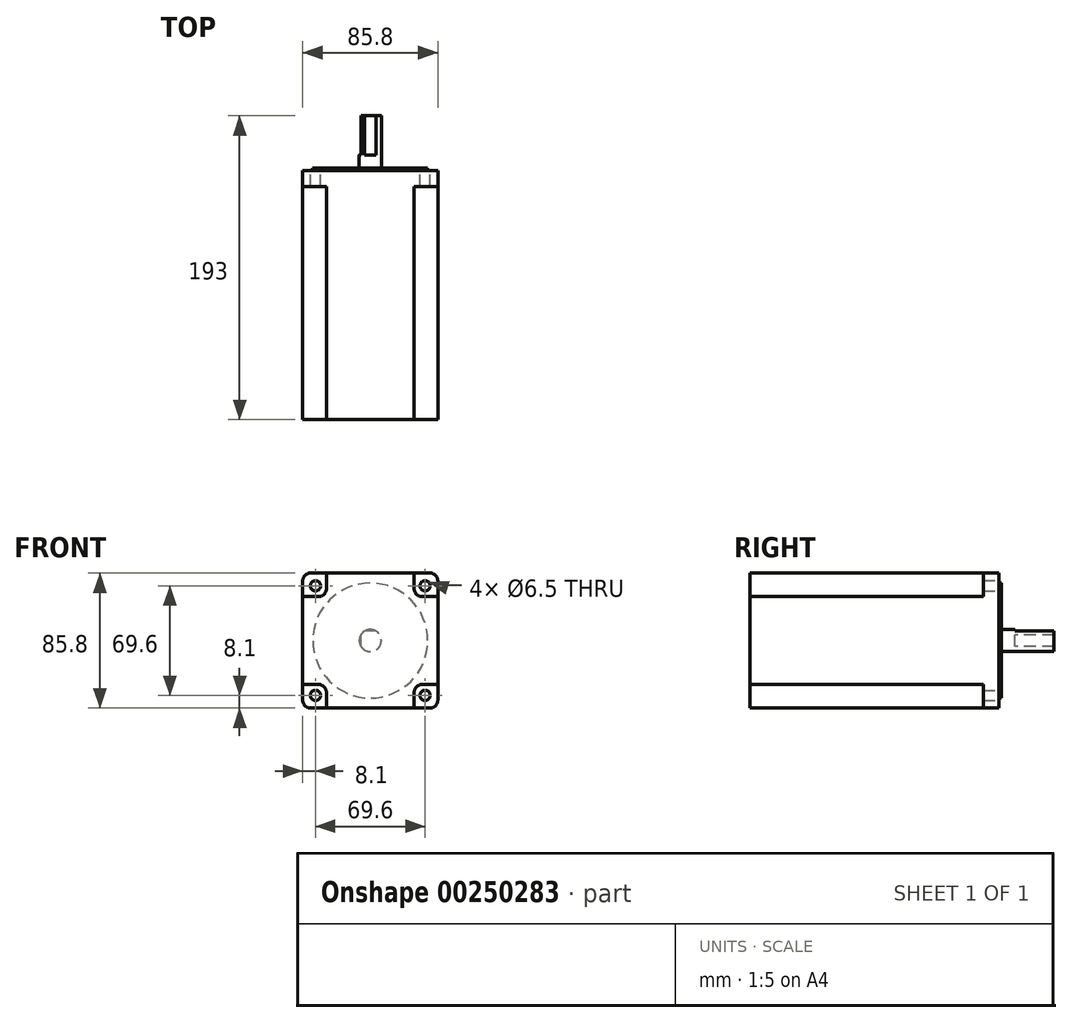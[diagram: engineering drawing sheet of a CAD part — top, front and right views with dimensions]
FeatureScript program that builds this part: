
annotation { "Feature Type Name" : "Feature", "Feature Type Description" : "" }
export const myFeature = defineFeature(function(context is Context, id is Id, definition is map)
    precondition{}
    {
        {
            var Q0;
            Q0=qCreatedBy(makeId("Front.planeOp"),FACE);
            var sketch = newSketch(context, id + "F0", { "sketchPlane" : qUnion([Q0])});
            skLineSegment(sketch, "E0.bottom", {"start": v(-37.9, 42.9) * mm, "end": v(37.9, 42.9) * mm});
            skLineSegment(sketch, "E0.top", {"start": v(-37.9, -42.9) * mm, "end": v(37.9, -42.9) * mm});
            skLineSegment(sketch, "E0.left", {"start": v(-42.9, 37.9) * mm, "end": v(-42.9, -37.9) * mm});
            skLineSegment(sketch, "E0.right", {"start": v(42.9, 37.9) * mm, "end": v(42.9, -37.9) * mm});
            skArc(sketch, "E1.filletArc", {"start": v(-42.9, -37.9) * mm, "mid": v(-41.44, -41.44) * mm, "end": v(-37.9, -42.9) * mm});
            skPoint(sketch, "E2.visualSharp", {"position": v(-42.9, 42.9) * mm});
            skArc(sketch, "E2.filletArc", {"start": v(-37.9, 42.9) * mm, "mid": v(-41.44, 41.44) * mm, "end": v(-42.9, 37.9) * mm});
            skPoint(sketch, "E3.visualSharp", {"position": v(42.9, 42.9) * mm});
            skArc(sketch, "E3.filletArc", {"start": v(42.9, 37.9) * mm, "mid": v(41.44, 41.44) * mm, "end": v(37.9, 42.9) * mm});
            skPoint(sketch, "E4.visualSharp", {"position": v(42.9, -42.9) * mm});
            skArc(sketch, "E4.filletArc", {"start": v(37.9, -42.9) * mm, "mid": v(41.44, -41.44) * mm, "end": v(42.9, -37.9) * mm});
            skSolve(sketch);
        }
        {
            var Q0;
            Q0=makeQuery(id+"F0.imprint","IMPRINT",FACE,{"disambiguationData":[TD([[makeQuery(id+"F0.imprint","IMPRINT",EDGE,{"derivedFrom":sQuery(id+"F0.wireOp",EDGE,"E0.bottom")}),-1.0]])]});
            extrude(context, id + "F1", {"entities" : qUnion([Q0]), "depth" : 158 * mm});
        }
        {
            var Q0;
            Q0=makeQuery(id+"F1.opExtrude","CAP_FACE",FACE,{"disambiguationData":[OSD([sQuery(id+"F0.wireOp",EDGE,"E0.bottom"),sQuery(id+"F0.wireOp",EDGE,"E0.top"),sQuery(id+"F0.wireOp",EDGE,"E0.left"),sQuery(id+"F0.wireOp",EDGE,"E0.right"),sQuery(id+"F0.wireOp",EDGE,"E1.filletArc"),sQuery(id+"F0.wireOp",EDGE,"E2.filletArc"),sQuery(id+"F0.wireOp",EDGE,"E3.filletArc"),sQuery(id+"F0.wireOp",EDGE,"E4.filletArc")])],"isStart":false});
            var sketch = newSketch(context, id + "F2", { "sketchPlane" : qUnion([Q0])});
            skLineSegment(sketch, "E5.bottom", {"start": v(27.9, 42.9) * mm, "end": v(42.9, 42.9) * mm});
            skLineSegment(sketch, "E5.top", {"start": v(27.9, 27.9) * mm, "end": v(42.9, 27.9) * mm});
            skLineSegment(sketch, "E5.left", {"start": v(27.9, 42.9) * mm, "end": v(27.9, 27.9) * mm});
            skLineSegment(sketch, "E5.right", {"start": v(42.9, 42.9) * mm, "end": v(42.9, 27.9) * mm});
            skLineSegment(sketch, "E6.MirrorCS", {"start": v(-27.9, 42.9) * mm, "end": v(-42.9, 42.9) * mm});
            skLineSegment(sketch, "E7.MirrorCS", {"start": v(-27.9, 27.9) * mm, "end": v(-42.9, 27.9) * mm});
            skLineSegment(sketch, "E8.MirrorCS", {"start": v(-42.9, 42.9) * mm, "end": v(-42.9, 27.9) * mm});
            skLineSegment(sketch, "E9.MirrorCS", {"start": v(-27.9, 42.9) * mm, "end": v(-27.9, 27.9) * mm});
            skLineSegment(sketch, "E10.MirrorCS", {"start": v(-27.9, -42.9) * mm, "end": v(-27.9, -27.9) * mm});
            skLineSegment(sketch, "E11.MirrorCS", {"start": v(-27.9, -42.9) * mm, "end": v(-42.9, -42.9) * mm});
            skLineSegment(sketch, "E12.MirrorCS", {"start": v(-27.9, -27.9) * mm, "end": v(-42.9, -27.9) * mm});
            skLineSegment(sketch, "E13.MirrorCS", {"start": v(-42.9, -42.9) * mm, "end": v(-42.9, -27.9) * mm});
            skLineSegment(sketch, "E14.MirrorCS", {"start": v(42.9, -42.9) * mm, "end": v(42.9, -27.9) * mm});
            skLineSegment(sketch, "E15.MirrorCS", {"start": v(27.9, -27.9) * mm, "end": v(42.9, -27.9) * mm});
            skLineSegment(sketch, "E16.MirrorCS", {"start": v(27.9, -42.9) * mm, "end": v(42.9, -42.9) * mm});
            skLineSegment(sketch, "E17.MirrorCS", {"start": v(27.9, -42.9) * mm, "end": v(27.9, -27.9) * mm});
            skSolve(sketch);
        }
        {
            var Q0;
            Q0=qSketchRegion(id+"F2",true);
            var Q1;
            Q1=makeQuery(id+"F1.opExtrude","CAP_FACE",FACE,{"disambiguationData":[OSD([sQuery(id+"F0.wireOp",EDGE,"E0.bottom"),sQuery(id+"F0.wireOp",EDGE,"E0.top"),sQuery(id+"F0.wireOp",EDGE,"E0.left"),sQuery(id+"F0.wireOp",EDGE,"E0.right"),sQuery(id+"F0.wireOp",EDGE,"E1.filletArc"),sQuery(id+"F0.wireOp",EDGE,"E2.filletArc"),sQuery(id+"F0.wireOp",EDGE,"E3.filletArc"),sQuery(id+"F0.wireOp",EDGE,"E4.filletArc")])],"isStart":false});
            extrude(context, id + "F3", {"entities" : qUnion([Q0]), "operationType" : NewBodyOperationType.REMOVE, "oppositeDirection" : true, "endBoundEntityFace" : qUnion([Q1]), "depth" : 148 * mm});
        }
        {
            var Q0;
            Q0=makeQuery(id+"F1.opExtrude","CAP_FACE",FACE,{"disambiguationData":[OSD([sQuery(id+"F0.wireOp",EDGE,"E0.bottom"),sQuery(id+"F0.wireOp",EDGE,"E0.top"),sQuery(id+"F0.wireOp",EDGE,"E0.left"),sQuery(id+"F0.wireOp",EDGE,"E0.right"),sQuery(id+"F0.wireOp",EDGE,"E1.filletArc"),sQuery(id+"F0.wireOp",EDGE,"E2.filletArc"),sQuery(id+"F0.wireOp",EDGE,"E3.filletArc"),sQuery(id+"F0.wireOp",EDGE,"E4.filletArc")])],"isStart":true});
            var sketch = newSketch(context, id + "F4", { "sketchPlane" : qUnion([Q0])});
            skCircle(sketch, "E18", {"center": v(34.8, 34.8) * mm, "radius": 3.25 * mm});
            skCircle(sketch, "E19.MirrorC", {"center": v(-34.8, 34.8) * mm, "radius": 3.25 * mm});
            skCircle(sketch, "E20.MirrorC", {"center": v(34.8, -34.8) * mm, "radius": 3.25 * mm});
            skCircle(sketch, "E21.MirrorC", {"center": v(-34.8, -34.8) * mm, "radius": 3.25 * mm});
            skSolve(sketch);
        }
        {
            var Q0;
            Q0=qSketchRegion(id+"F4",true);
            extrude(context, id + "F5", {"entities" : qUnion([Q0]), "operationType" : NewBodyOperationType.REMOVE, "endBound" : BoundingType.UP_TO_NEXT, "oppositeDirection" : true, "depth" : 25 * mm});
        }
        {
            var Q0;
            Q0=makeQuery(id+"F3.boolean.opBoolean","COPY",EDGE,{"derivedFrom":makeQuery(id+"F3.opExtrude","SWEPT_EDGE",EDGE,{"disambiguationData":[OSD([sQuery(id+"F0.wireOp",EDGE,"E0.left"),sQuery(id+"F2.wireOp",EDGE,"E8.MirrorCS"),sQuery(id+"F2.wireOp",EDGE,"E7.MirrorCS")])]})});
            var Q1;
            Q1=makeQuery(id+"F3.boolean.opBoolean","COPY",EDGE,{"derivedFrom":makeQuery(id+"F3.opExtrude","SWEPT_EDGE",EDGE,{"disambiguationData":[OSD([sQuery(id+"F0.wireOp",EDGE,"E0.left"),sQuery(id+"F2.wireOp",EDGE,"E13.MirrorCS"),sQuery(id+"F2.wireOp",EDGE,"E12.MirrorCS")])]})});
            var Q2;
            Q2=makeQuery(id+"F3.boolean.opBoolean","COPY",EDGE,{"derivedFrom":makeQuery(id+"F3.opExtrude","SWEPT_EDGE",EDGE,{"disambiguationData":[OSD([sQuery(id+"F2.wireOp",EDGE,"E12.MirrorCS"),sQuery(id+"F2.wireOp",EDGE,"E10.MirrorCS")])]})});
            var Q3;
            Q3=makeQuery(id+"F3.boolean.opBoolean","COPY",EDGE,{"derivedFrom":makeQuery(id+"F3.opExtrude","SWEPT_EDGE",EDGE,{"disambiguationData":[OSD([sQuery(id+"F0.wireOp",EDGE,"E0.top"),sQuery(id+"F2.wireOp",EDGE,"E10.MirrorCS"),sQuery(id+"F2.wireOp",EDGE,"E11.MirrorCS")])]})});
            var Q4;
            Q4=makeQuery(id+"F3.boolean.opBoolean","COPY",EDGE,{"derivedFrom":makeQuery(id+"F3.opExtrude","SWEPT_EDGE",EDGE,{"disambiguationData":[OSD([sQuery(id+"F0.wireOp",EDGE,"E0.top"),sQuery(id+"F2.wireOp",EDGE,"E17.MirrorCS"),sQuery(id+"F2.wireOp",EDGE,"E16.MirrorCS")])]})});
            var Q5;
            Q5=makeQuery(id+"F3.boolean.opBoolean","COPY",EDGE,{"derivedFrom":makeQuery(id+"F3.opExtrude","SWEPT_EDGE",EDGE,{"disambiguationData":[OSD([sQuery(id+"F0.wireOp",EDGE,"E0.bottom"),sQuery(id+"F2.wireOp",EDGE,"E9.MirrorCS"),sQuery(id+"F2.wireOp",EDGE,"E6.MirrorCS")])]})});
            var Q6;
            Q6=makeQuery(id+"F3.boolean.opBoolean","COPY",EDGE,{"derivedFrom":makeQuery(id+"F3.opExtrude","SWEPT_EDGE",EDGE,{"disambiguationData":[OSD([sQuery(id+"F2.wireOp",EDGE,"E17.MirrorCS"),sQuery(id+"F2.wireOp",EDGE,"E15.MirrorCS")])]})});
            var Q7;
            Q7=makeQuery(id+"F3.boolean.opBoolean","COPY",EDGE,{"derivedFrom":makeQuery(id+"F3.opExtrude","SWEPT_EDGE",EDGE,{"disambiguationData":[OSD([sQuery(id+"F0.wireOp",EDGE,"E0.right"),sQuery(id+"F2.wireOp",EDGE,"E14.MirrorCS"),sQuery(id+"F2.wireOp",EDGE,"E15.MirrorCS")])]})});
            var Q8;
            Q8=makeQuery(id+"F3.boolean.opBoolean","COPY",EDGE,{"derivedFrom":makeQuery(id+"F3.opExtrude","SWEPT_EDGE",EDGE,{"disambiguationData":[OSD([sQuery(id+"F0.wireOp",EDGE,"E0.right"),sQuery(id+"F2.wireOp",EDGE,"E5.right"),sQuery(id+"F2.wireOp",EDGE,"E5.top")])]})});
            var Q9;
            Q9=makeQuery(id+"F3.boolean.opBoolean","COPY",EDGE,{"derivedFrom":makeQuery(id+"F3.opExtrude","SWEPT_EDGE",EDGE,{"disambiguationData":[OSD([sQuery(id+"F0.wireOp",EDGE,"E0.bottom"),sQuery(id+"F2.wireOp",EDGE,"E5.bottom"),sQuery(id+"F2.wireOp",EDGE,"E5.left")])]})});
            var Q10;
            Q10=makeQuery(id+"F3.boolean.opBoolean","COPY",EDGE,{"derivedFrom":makeQuery(id+"F3.opExtrude","SWEPT_EDGE",EDGE,{"disambiguationData":[OSD([sQuery(id+"F2.wireOp",EDGE,"E5.top"),sQuery(id+"F2.wireOp",EDGE,"E5.left")])]})});
            var Q11;
            Q11=makeQuery(id+"F3.boolean.opBoolean","COPY",EDGE,{"derivedFrom":makeQuery(id+"F3.opExtrude","SWEPT_EDGE",EDGE,{"disambiguationData":[OSD([sQuery(id+"F2.wireOp",EDGE,"E9.MirrorCS"),sQuery(id+"F2.wireOp",EDGE,"E7.MirrorCS")])]})});
            fillet(context, id + "F6", {"entities" : qUnion([Q0, Q1, Q2, Q3, Q4, Q5, Q6, Q7, Q8, Q9, Q10, Q11]), "radius" : 5 * mm, "tangentPropagation" : true, "allowEdgeOverflow" : false});
        }
        {
            var Q0;
            Q0=makeQuery(id+"F1.opExtrude","CAP_FACE",FACE,{"disambiguationData":[OSD([sQuery(id+"F0.wireOp",EDGE,"E0.bottom"),sQuery(id+"F0.wireOp",EDGE,"E0.top"),sQuery(id+"F0.wireOp",EDGE,"E0.left"),sQuery(id+"F0.wireOp",EDGE,"E0.right"),sQuery(id+"F0.wireOp",EDGE,"E1.filletArc"),sQuery(id+"F0.wireOp",EDGE,"E2.filletArc"),sQuery(id+"F0.wireOp",EDGE,"E3.filletArc"),sQuery(id+"F0.wireOp",EDGE,"E4.filletArc")])],"isStart":true});
            var sketch = newSketch(context, id + "F7", { "sketchPlane" : qUnion([Q0])});
            skCircle(sketch, "E22", {"center": v(0, 0) * mm, "radius": 36.5 * mm});
            skSolve(sketch);
        }
        {
            var Q0;
            Q0=qSketchRegion(id+"F7",true);
            extrude(context, id + "F8", {"entities" : qUnion([Q0]), "operationType" : NewBodyOperationType.ADD, "depth" : 1.6 * mm});
        }
        {
            var Q0;
            Q0=makeQuery(id+"F1.opExtrude","CAP_FACE",FACE,{"disambiguationData":[OSD([sQuery(id+"F0.wireOp",EDGE,"E0.bottom"),sQuery(id+"F0.wireOp",EDGE,"E0.top"),sQuery(id+"F0.wireOp",EDGE,"E0.left"),sQuery(id+"F0.wireOp",EDGE,"E0.right"),sQuery(id+"F0.wireOp",EDGE,"E1.filletArc"),sQuery(id+"F0.wireOp",EDGE,"E2.filletArc"),sQuery(id+"F0.wireOp",EDGE,"E3.filletArc"),sQuery(id+"F0.wireOp",EDGE,"E4.filletArc")])],"isStart":true});
            var sketch = newSketch(context, id + "F9", { "sketchPlane" : qUnion([Q0])});
            skCircle(sketch, "E23", {"center": v(0, 0) * mm, "radius": 7 * mm});
            skSolve(sketch);
        }
        {
            var Q0;
            Q0=qSketchRegion(id+"F9",true);
            var Q1;
            Q1=sQuery(id+"F9.wireOp",EDGE,"E23");
            extrude(context, id + "F10", {"entities" : qUnion([Q0]), "surfaceEntities" : qUnion([Q1]), "depth" : 35 * mm});
        }
        {
            var Q0;
            Q0=makeQuery(id+"F10.opExtrude","CAP_FACE",FACE,{"disambiguationData":[OSD([sQuery(id+"F9.wireOp",EDGE,"E23")])],"isStart":false});
            var sketch = newSketch(context, id + "F11", { "sketchPlane" : qUnion([Q0])});
            skLineSegment(sketch, "E24", {"start": v(-14.54, 6) * mm, "end": v(6, 6) * mm});
            skLineSegment(sketch, "E25", {"start": v(6, -12.05) * mm, "end": v(6, 6) * mm});
            skLineSegment(sketch, "E26", {"start": v(-14.54, 6) * mm, "end": v(-14.54, 12.76) * mm});
            skLineSegment(sketch, "E27", {"start": v(-14.54, 12.76) * mm, "end": v(13.2, 12.76) * mm});
            skLineSegment(sketch, "E28", {"start": v(13.2, 12.76) * mm, "end": v(13.2, -12.47) * mm});
            skLineSegment(sketch, "E29", {"start": v(13.2, -12.47) * mm, "end": v(6, -12.05) * mm});
            skSolve(sketch);
        }
        {
            var Q0;
            Q0=qSketchRegion(id+"F11",true);
            extrude(context, id + "F12", {"entities" : qUnion([Q0]), "operationType" : NewBodyOperationType.REMOVE, "oppositeDirection" : true, "depth" : 25 * mm});
        }
    });
